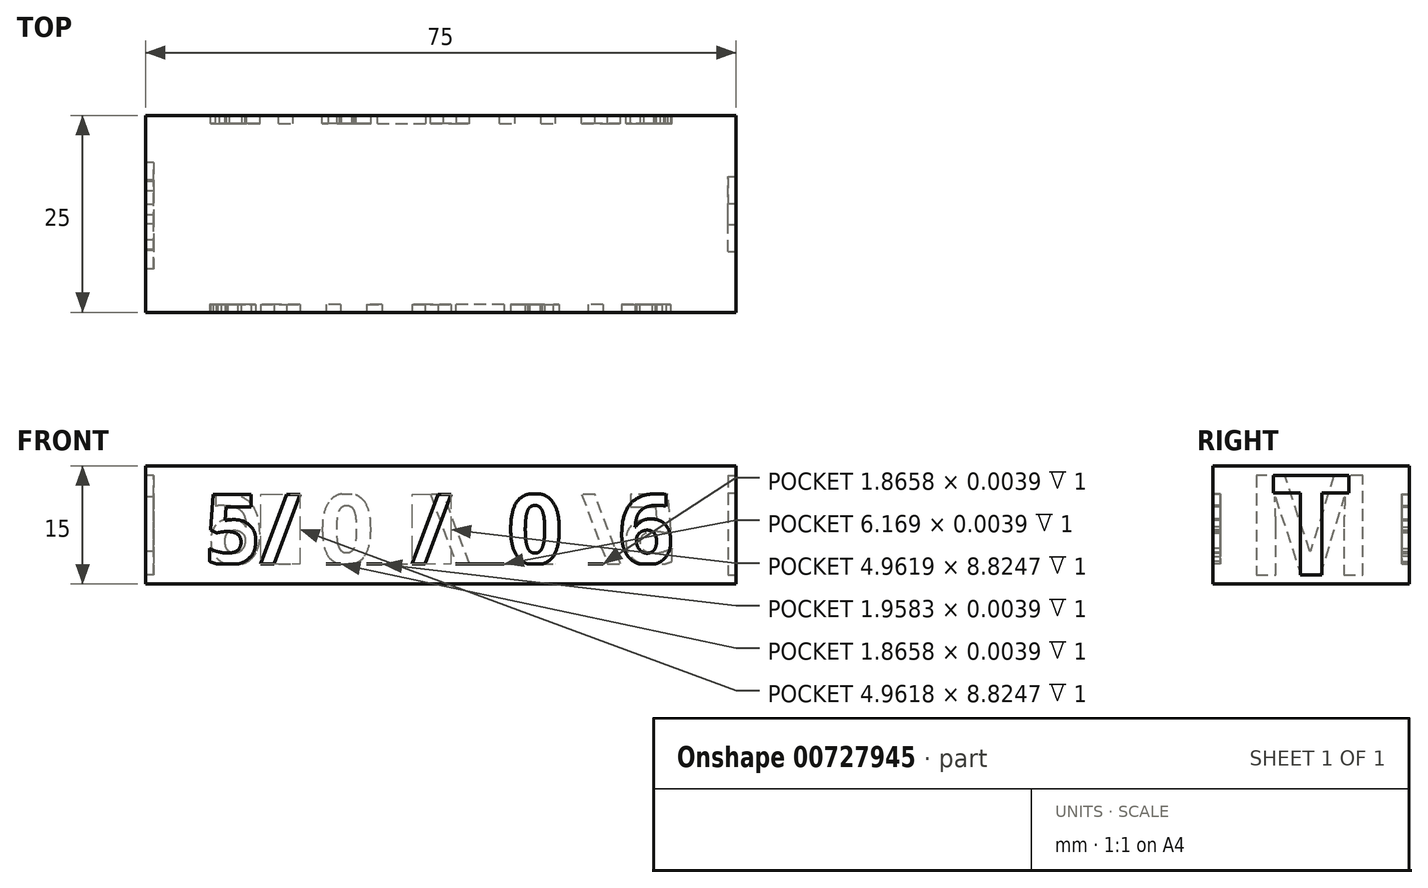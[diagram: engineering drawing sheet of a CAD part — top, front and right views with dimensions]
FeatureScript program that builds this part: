
annotation { "Feature Type Name" : "Feature", "Feature Type Description" : "" }
export const myFeature = defineFeature(function(context is Context, id is Id, definition is map)
    precondition{}
    {
        {
            var Q0;
            Q0=qCreatedBy(makeId("Top.planeOp"),FACE);
            var sketch = newSketch(context, id + "F0", { "sketchPlane" : qUnion([Q0])});
            skLineSegment(sketch, "E0.bottom", {"start": v(0, 0) * mm, "end": v(75, 0) * mm});
            skLineSegment(sketch, "E0.top", {"start": v(0, -25) * mm, "end": v(75, -25) * mm});
            skLineSegment(sketch, "E0.left", {"start": v(0, 0) * mm, "end": v(0, -25) * mm});
            skLineSegment(sketch, "E0.right", {"start": v(75, 0) * mm, "end": v(75, -25) * mm});
            skSolve(sketch);
        }
        {
            var Q0;
            Q0=qSketchRegion(id+"F0",true);
            extrude(context, id + "F10", {"entities" : qUnion([Q0]), "depth" : 15 * mm});
        }
        {
            var Q0;
            Q0=makeQuery(id+"F10.opExtrude","SWEPT_FACE",FACE,{"disambiguationData":[OSD([sQuery(id+"F0.wireOp",EDGE,"E0.top")])]});
            var sketch = newSketch(context, id + "F1", { "sketchPlane" : qUnion([Q0])});
            skLineSegment(sketch, "E1.bottom", {"start": v(7.5, 11.43) * mm, "end": v(67.5, 11.43) * mm});
            skLineSegment(sketch, "E1.top", {"start": v(7.5, 2.53) * mm, "end": v(67.5, 2.53) * mm});
            skLineSegment(sketch, "E1.left", {"start": v(7.5, 11.43) * mm, "end": v(7.5, 2.53) * mm});
            skLineSegment(sketch, "E1.right", {"start": v(67.5, 11.43) * mm, "end": v(67.5, 2.53) * mm});
            skPoint(sketch, "E1.middle", {"position": v(37.5, 6.98) * mm});
            skText(sketch, "E2", { "text": "5/17/2016", "fontName": "OpenSans-Bold.ttf"});
            const initialGuessF1  = {"E2": [0.0075, 0.00253, 1, 0, 0.0089]};
            skSetInitialGuess(sketch, initialGuessF1);
            skSolve(sketch);
        }
        {
            var Q0;
            Q0=makeQuery(id+"F10.opExtrude","SWEPT_FACE",FACE,{"disambiguationData":[OSD([sQuery(id+"F0.wireOp",EDGE,"E0.bottom")])]});
            var sketch = newSketch(context, id + "F2", { "sketchPlane" : qUnion([Q0])});
            skLineSegment(sketch, "E3.0", {"start": v(-67.5, 11.43) * mm, "end": v(-67.5, 2.53) * mm});
            skLineSegment(sketch, "E3.1", {"start": v(-7.5, 11.43) * mm, "end": v(-67.5, 11.43) * mm});
            skLineSegment(sketch, "E3.2", {"start": v(-7.5, 2.53) * mm, "end": v(-67.5, 2.53) * mm});
            skLineSegment(sketch, "E3.3", {"start": v(-7.5, 11.43) * mm, "end": v(-7.5, 2.53) * mm});
            skText(sketch, "E4", { "text": "5/17/2016", "fontName": "OpenSans-Bold.ttf"});
            const initialGuessF2  = {"E4": [-0.0675, 0.00253, 1, 0, 0.0089]};
            skSetInitialGuess(sketch, initialGuessF2);
            skSolve(sketch);
        }
        {
            var Q0;
            Q0=makeQuery(id+"F2.imprint","IMPRINT",FACE,{"disambiguationData":[TD([[makeQuery(id+"F2.imprint","IMPRINT",EDGE,{"derivedFrom":sQuery(id+"F2.wireOp",EDGE,"E4.sketch_text.stroke-24")}),-1.0]])]});
            var Q1;
            Q1=makeQuery(id+"F2.imprint","IMPRINT",FACE,{"disambiguationData":[TD([[makeQuery(id+"F2.imprint","IMPRINT",EDGE,{"derivedFrom":sQuery(id+"F2.wireOp",EDGE,"E4.sketch_text.stroke-0")}),-1.0]])]});
            var Q2;
            Q2=makeQuery(id+"F2.imprint","IMPRINT",FACE,{"disambiguationData":[TD([[makeQuery(id+"F2.imprint","IMPRINT",EDGE,{"derivedFrom":sQuery(id+"F2.wireOp",EDGE,"E4.sketch_text.stroke-20")}),-1.0]])]});
            var Q3;
            Q3=makeQuery(id+"F2.imprint","IMPRINT",FACE,{"disambiguationData":[TD([[makeQuery(id+"F2.imprint","IMPRINT",EDGE,{"derivedFrom":sQuery(id+"F2.wireOp",EDGE,"E4.sketch_text.stroke-34")}),-1.0]])]});
            var Q4;
            Q4=makeQuery(id+"F2.imprint","IMPRINT",FACE,{"disambiguationData":[TD([[makeQuery(id+"F2.imprint","IMPRINT",EDGE,{"derivedFrom":sQuery(id+"F2.wireOp",EDGE,"E4.sketch_text.stroke-41")}),-1.0]])]});
            var Q5;
            Q5=makeQuery(id+"F2.imprint","IMPRINT",FACE,{"disambiguationData":[TD([[makeQuery(id+"F2.imprint","IMPRINT",EDGE,{"derivedFrom":sQuery(id+"F2.wireOp",EDGE,"E4.sketch_text.stroke-45")}),-1.0]])]});
            var Q6;
            {var subQ12=sQuery(id+"F2.wireOp",EDGE,"E4.sketch_text.stroke-69");Q6=makeQuery(id+"F2.imprint","IMPRINT",FACE,{"disambiguationData":[TD([[makeQuery(id+"F2.imprint","IMPRINT",EDGE,{"derivedFrom":subQ12}),-1.0]])]});}
            var Q7;
            Q7=makeQuery(id+"F2.imprint","IMPRINT",FACE,{"disambiguationData":[TD([[makeQuery(id+"F2.imprint","IMPRINT",EDGE,{"derivedFrom":sQuery(id+"F2.wireOp",EDGE,"E4.sketch_text.stroke-85")}),-1.0]])]});
            var Q8;
            {var subQ10=sQuery(id+"F2.wireOp",EDGE,"E4.sketch_text.stroke-95");Q8=makeQuery(id+"F2.imprint","IMPRINT",FACE,{"disambiguationData":[TD([[makeQuery(id+"F2.imprint","IMPRINT",EDGE,{"derivedFrom":subQ10}),-1.0]])]});}
            extrude(context, id + "F3", {"entities" : qUnion([Q0, Q1, Q2, Q3, Q4, Q5, Q6, Q7, Q8]), "operationType" : NewBodyOperationType.REMOVE, "depth" : -1 * mm, "offsetDistance" : 25 * mm});
        }
        {
            var Q0;
            Q0=makeQuery(id+"F1.imprint","IMPRINT",FACE,{"disambiguationData":[TD([[makeQuery(id+"F1.imprint","IMPRINT",EDGE,{"derivedFrom":sQuery(id+"F1.wireOp",EDGE,"E2.sketch_text.stroke-0")}),-1.0]])]});
            var Q1;
            Q1=makeQuery(id+"F1.imprint","IMPRINT",FACE,{"disambiguationData":[TD([[makeQuery(id+"F1.imprint","IMPRINT",EDGE,{"derivedFrom":sQuery(id+"F1.wireOp",EDGE,"E2.sketch_text.stroke-20")}),-1.0]])]});
            var Q2;
            Q2=makeQuery(id+"F1.imprint","IMPRINT",FACE,{"disambiguationData":[TD([[makeQuery(id+"F1.imprint","IMPRINT",EDGE,{"derivedFrom":sQuery(id+"F1.wireOp",EDGE,"E2.sketch_text.stroke-24")}),-1.0]])]});
            var Q3;
            Q3=makeQuery(id+"F1.imprint","IMPRINT",FACE,{"disambiguationData":[TD([[makeQuery(id+"F1.imprint","IMPRINT",EDGE,{"derivedFrom":sQuery(id+"F1.wireOp",EDGE,"E2.sketch_text.stroke-34")}),-1.0]])]});
            var Q4;
            Q4=makeQuery(id+"F1.imprint","IMPRINT",FACE,{"disambiguationData":[TD([[makeQuery(id+"F1.imprint","IMPRINT",EDGE,{"derivedFrom":sQuery(id+"F1.wireOp",EDGE,"E2.sketch_text.stroke-41")}),-1.0]])]});
            var Q5;
            Q5=makeQuery(id+"F1.imprint","IMPRINT",FACE,{"disambiguationData":[TD([[makeQuery(id+"F1.imprint","IMPRINT",EDGE,{"derivedFrom":sQuery(id+"F1.wireOp",EDGE,"E2.sketch_text.stroke-45")}),-1.0]])]});
            var Q6;
            {var subQ11=sQuery(id+"F1.wireOp",EDGE,"E2.sketch_text.stroke-69");Q6=makeQuery(id+"F1.imprint","IMPRINT",FACE,{"disambiguationData":[TD([[makeQuery(id+"F1.imprint","IMPRINT",EDGE,{"derivedFrom":subQ11}),-1.0]])]});}
            var Q7;
            Q7=makeQuery(id+"F1.imprint","IMPRINT",FACE,{"disambiguationData":[TD([[makeQuery(id+"F1.imprint","IMPRINT",EDGE,{"derivedFrom":sQuery(id+"F1.wireOp",EDGE,"E2.sketch_text.stroke-85")}),-1.0]])]});
            var Q8;
            {var subQ10=sQuery(id+"F1.wireOp",EDGE,"E2.sketch_text.stroke-95");Q8=makeQuery(id+"F1.imprint","IMPRINT",FACE,{"disambiguationData":[TD([[makeQuery(id+"F1.imprint","IMPRINT",EDGE,{"derivedFrom":subQ10}),-1.0]])]});}
            extrude(context, id + "F4", {"entities" : qUnion([Q0, Q1, Q2, Q3, Q4, Q5, Q6, Q7, Q8]), "operationType" : NewBodyOperationType.REMOVE, "oppositeDirection" : true, "depth" : 1 * mm, "offsetDistance" : 25 * mm});
        }
        {
            var Q0;
            Q0=makeQuery(id+"F10.opExtrude","SWEPT_FACE",FACE,{"disambiguationData":[OSD([sQuery(id+"F0.wireOp",EDGE,"E0.left")])]});
            var sketch = newSketch(context, id + "F5", { "sketchPlane" : qUnion([Q0])});
            skLineSegment(sketch, "E5.bottom", {"start": v(4.36, 13.88) * mm, "end": v(20.64, 13.88) * mm});
            skLineSegment(sketch, "E5.top", {"start": v(4.36, 1.12) * mm, "end": v(20.64, 1.12) * mm});
            skLineSegment(sketch, "E5.left", {"start": v(4.36, 13.88) * mm, "end": v(4.36, 1.12) * mm});
            skLineSegment(sketch, "E5.right", {"start": v(20.64, 13.88) * mm, "end": v(20.64, 1.12) * mm});
            skPoint(sketch, "E5.middle", {"position": v(12.5, 7.5) * mm});
            skText(sketch, "E6", { "text": "M", "fontName": "OpenSans-Bold.ttf"});
            skLineSegment(sketch, "E7", {"start": v(12.5, 15) * mm, "end": v(12.5, 0) * mm});
            const initialGuessF5  = {"E6": [0.00436, 0.00112, 1, 0, 0.01277]};
            skSetInitialGuess(sketch, initialGuessF5);
            skSolve(sketch);
        }
        {
            var Q0;
            {var subQ5=sQuery(id+"F5.wireOp",EDGE,"E6.sketch_text.stroke-0");Q0=makeQuery(id+"F5.imprint","IMPRINT",FACE,{"disambiguationData":[TD([[makeQuery(id+"F5.imprint","IMPRINT",EDGE,{"derivedFrom":subQ5}),-1.0]])]});}
            var Q1;
            {var subQ0=sQuery(id+"F5.wireOp",EDGE,"E6.sketch_text.stroke-8");Q1=makeQuery(id+"F5.imprint","IMPRINT",FACE,{"disambiguationData":[TD([[makeQuery(id+"F5.imprint","IMPRINT",EDGE,{"derivedFrom":subQ0}),-1.0]])]});}
            extrude(context, id + "F6", {"entities" : qUnion([Q0, Q1]), "operationType" : NewBodyOperationType.REMOVE, "oppositeDirection" : true, "depth" : 1 * mm, "offsetDistance" : 25 * mm});
        }
        {
            var Q0;
            Q0=makeQuery(id+"F10.opExtrude","SWEPT_FACE",FACE,{"disambiguationData":[OSD([sQuery(id+"F0.wireOp",EDGE,"E0.right")])]});
            var sketch = newSketch(context, id + "F7", { "sketchPlane" : qUnion([Q0])});
            skLineSegment(sketch, "E8.4", {"start": v(-20.64, 13.88) * mm, "end": v(-20.64, 1.12) * mm});
            skPoint(sketch, "E8.5", {"position": v(-12.5, 7.5) * mm});
            skLineSegment(sketch, "E8.6", {"start": v(-12.5, 15) * mm, "end": v(-12.5, 0) * mm});
            skText(sketch, "E9", { "text": "T", "fontName": "OpenSans-Bold.ttf"});
            const initialGuessF7  = {"E9": [-0.02064, 0.00112, 1, 0, 0.01277]};
            skSetInitialGuess(sketch, initialGuessF7);
            skSolve(sketch);
        }
        {
            var Q0;
            Q0=makeQuery(id+"F7.imprint","IMPRINT",FACE,{"disambiguationData":[TD([[makeQuery(id+"F7.imprint","IMPRINT",EDGE,{"derivedFrom":sQuery(id+"F7.wireOp",EDGE,"E9.sketch_text.stroke-0")}),1.0]])]});
            var sketch = newSketch(context, id + "F8", { "sketchPlane" : qUnion([Q0])});
            skLineSegment(sketch, "E10.0.3", {"start": v(-17.28, 13.78) * mm, "end": v(-17.28, 11.54) * mm});
            skLineSegment(sketch, "E10.0.4", {"start": v(-17.28, 11.54) * mm, "end": v(-13.84, 11.54) * mm});
            skLineSegment(sketch, "E10.0.5", {"start": v(-13.84, 11.54) * mm, "end": v(-13.84, 1.12) * mm});
            skLineSegment(sketch, "E10.0.6", {"start": v(-13.84, 1.12) * mm, "end": v(-11.16, 1.12) * mm});
            skLineSegment(sketch, "E10.0.7", {"start": v(-11.16, 1.12) * mm, "end": v(-11.16, 11.54) * mm});
            skLineSegment(sketch, "E10.1.1", {"start": v(-7.72, 11.54) * mm, "end": v(-7.72, 13.78) * mm});
            skLineSegment(sketch, "E11", {"start": v(-17.28, 13.78) * mm, "end": v(-7.72, 13.78) * mm});
            skLineSegment(sketch, "E12", {"start": v(-7.72, 11.54) * mm, "end": v(-11.16, 11.54) * mm});
            skLineSegment(sketch, "E13", {"start": v(-12.5, 13.78) * mm, "end": v(-12.5, 1.12) * mm, "construction": true});
            skSolve(sketch);
        }
        {
            var Q0;
            Q0 = qSketchRegion(id + "F8", true);
            extrude(context, id + "F9", {"entities" : qUnion([Q0]), "operationType" : NewBodyOperationType.REMOVE, "oppositeDirection" : true, "depth" : 1 * mm, "offsetDistance" : 25 * mm});
        }
    });
